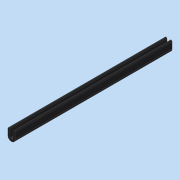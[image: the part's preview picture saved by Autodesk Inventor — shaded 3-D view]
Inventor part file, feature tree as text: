
AUTODESK INVENTOR PART (.ipt)
format: ipt  version: 2020 (Build 240168000, 168)  size: 90,624 bytes
history: native  units: mm
features: other x1, extrude x1
ambient origin geometry x8: Origin, YZ Plane, XZ Plane, XY Plane, X Axis, Y Axis, Z Axis, Center Point
bodies: Body1 (feature_tree)
feature tree (2):
  other  "實體1"
  extrude  "擠出1"  Depth=6.0mm
